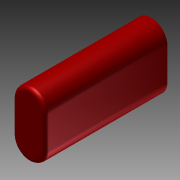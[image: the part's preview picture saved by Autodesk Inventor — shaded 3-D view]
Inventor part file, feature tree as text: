
AUTODESK INVENTOR PART (.ipt)
format: ipt  version: 2013 (Build 170138000, 138)  size: 89,088 bytes
history: native  units: mm (DEFAULTED — no unit token found)
features: extrude x1, fillet x1, sketch x1, reference x1
ambient origin geometry x8: Origin, YZ Plane, XZ Plane, XY Plane, X Axis, Y Axis, Z Axis, Center Point
bodies: Solid1 (feature_tree)
feature tree (4):
  extrude  "Extrusion1"  Depth=0.381mm
  fillet  "Fillet1"  [1 undecoded]
  sketch  "Sketch1"  dims[d0=12.7mm d1=0.0mm d2=0.381mm]
  reference  "Reference1"
note: 1 required parameter value undecoded (feature->parameter linkage not recoverable at this tier; creation-order binding heuristic only, values carry confidence <= 0.55)
